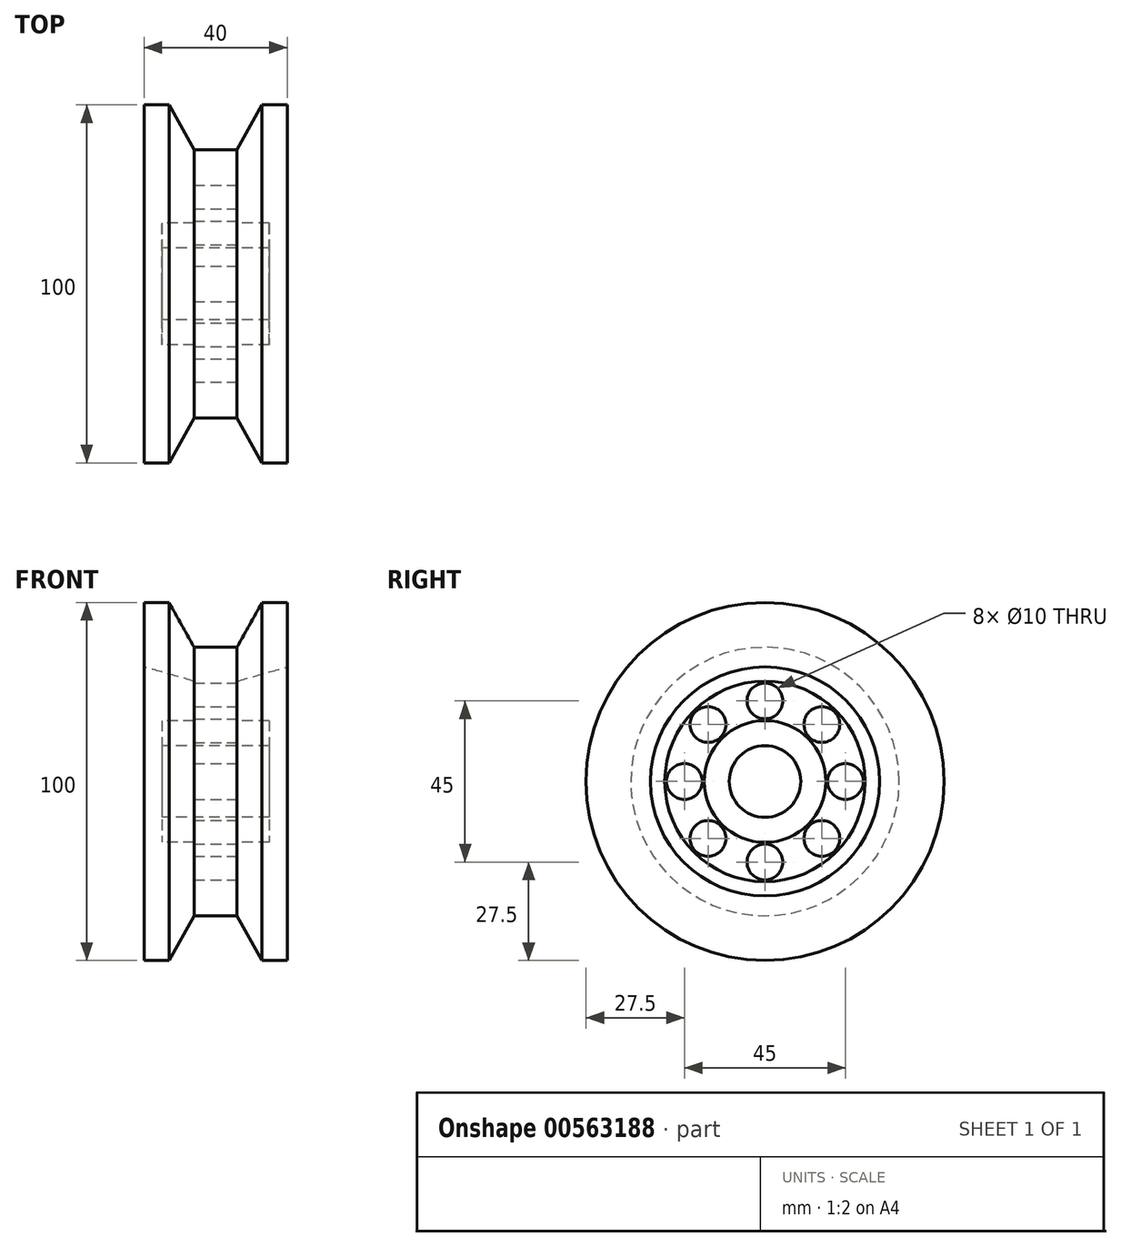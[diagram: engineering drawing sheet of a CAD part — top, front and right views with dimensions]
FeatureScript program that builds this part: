
annotation { "Feature Type Name" : "Feature", "Feature Type Description" : "" }
export const myFeature = defineFeature(function(context is Context, id is Id, definition is map)
    precondition{}
    {
        {
            var Q0;
            Q0=qCreatedBy(makeId("Front.planeOp"),FACE);
            var sketch = newSketch(context, id + "F0", { "sketchPlane" : qUnion([Q0])});
            skLineSegment(sketch, "E0", {"start": v(-20, 0) * mm, "end": v(-13, 0) * mm});
            skLineSegment(sketch, "E1", {"start": v(-20, 0) * mm, "end": v(-20, 18) * mm});
            skPoint(sketch, "E2", {"position": v(-13, 0) * mm});
            skLineSegment(sketch, "E3", {"start": v(-6, -5.42) * mm, "end": v(-6, 12.5) * mm, "construction": true});
            skPoint(sketch, "E4", {"position": v(-6, 0) * mm});
            skLineSegment(sketch, "E5", {"start": v(-13, 0) * mm, "end": v(-6, 12.5) * mm});
            skLineSegment(sketch, "E6", {"start": v(-6, 12.5) * mm, "end": v(0, 12.5) * mm});
            skLineSegment(sketch, "E7", {"start": v(-6, 12.5) * mm, "end": v(-6, 43.54) * mm, "construction": true});
            skPoint(sketch, "E8", {"position": v(-6, 22) * mm});
            skPoint(sketch, "E9", {"position": v(7.7, 57.87) * mm});
            skPoint(sketch, "E10", {"position": v(9.06, 58.61) * mm});
            skLineSegment(sketch, "E11", {"start": v(-20, 18) * mm, "end": v(-6, 22) * mm});
            skLineSegment(sketch, "E12", {"start": v(-6, 22) * mm, "end": v(0, 22) * mm});
            skLineSegment(sketch, "E13", {"start": v(-6, 22) * mm, "end": v(-6, 33) * mm});
            skLineSegment(sketch, "E14", {"start": v(-6, 33) * mm, "end": v(0, 33) * mm});
            skLineSegment(sketch, "E15", {"start": v(0, 33) * mm, "end": v(-15, 33) * mm});
            skLineSegment(sketch, "E16", {"start": v(-15, 33) * mm, "end": v(-15, 40) * mm});
            skLineSegment(sketch, "E17", {"start": v(-15, 40) * mm, "end": v(0, 40) * mm});
            skLineSegment(sketch, "E18.MirrorCS", {"start": v(15, 40) * mm, "end": v(0, 40) * mm});
            skLineSegment(sketch, "E19.MirrorCS", {"start": v(15, 33) * mm, "end": v(15, 40) * mm});
            skLineSegment(sketch, "E20.MirrorCS", {"start": v(0, 33) * mm, "end": v(15, 33) * mm});
            skLineSegment(sketch, "E21.MirrorCS", {"start": v(6, 12.5) * mm, "end": v(6, 43.54) * mm, "construction": true});
            skLineSegment(sketch, "E22.MirrorCS", {"start": v(6, 22) * mm, "end": v(0, 22) * mm});
            skLineSegment(sketch, "E23.MirrorCS", {"start": v(20, 18) * mm, "end": v(6, 22) * mm});
            skLineSegment(sketch, "E24.MirrorCS", {"start": v(6, 12.5) * mm, "end": v(0, 12.5) * mm});
            skLineSegment(sketch, "E25.MirrorCS", {"start": v(13, 0) * mm, "end": v(6, 12.5) * mm});
            skLineSegment(sketch, "E26.MirrorCS", {"start": v(20, 0) * mm, "end": v(20, 18) * mm});
            skPoint(sketch, "E27", {"position": v(6, 33) * mm});
            skLineSegment(sketch, "E28", {"start": v(6, 33) * mm, "end": v(6, 22) * mm});
            skLineSegment(sketch, "E29.trimOffspring", {"start": v(13, 0) * mm, "end": v(20, 0) * mm});
            skLineSegment(sketch, "E30", {"start": v(-64.97, 50) * mm, "end": v(56.77, 50) * mm, "construction": true});
            skPoint(sketch, "E31", {"position": v(0, 50) * mm});
            skSolve(sketch);
        }
        {
            var Q0;
            Q0=makeQuery(id+"F0.imprint","IMPRINT",FACE,{"disambiguationData":[TD([[makeQuery(id+"F0.imprint","IMPRINT",EDGE,{"derivedFrom":sQuery(id+"F0.wireOp",EDGE,"E0")}),1.0]])]});
            var Q1;
            Q1=makeQuery(id+"F0.imprint","IMPRINT",FACE,{"disambiguationData":[TD([[makeQuery(id+"F0.imprint","IMPRINT",EDGE,{"derivedFrom":sQuery(id+"F0.wireOp",EDGE,"E12")}),1.0]])]});
            var Q2;
            {var subQ0=sQuery(id+"F0.wireOp",EDGE,"E16");Q2=makeQuery(id+"F0.imprint","IMPRINT",FACE,{"disambiguationData":[TD([[makeQuery(id+"F0.imprint","IMPRINT",EDGE,{"derivedFrom":subQ0}),-1.0]])]});}
            var Q3;
            Q3=sQuery(id+"F0.wireOp",EDGE,"E30");
            revolve(context, id + "F1", {"entities" : qUnion([Q0, Q1, Q2]), "axis" : qUnion([Q3]), "revolveType" : RevolveType.FULL});
        }
        {
            var Q0;
            Q0=qCreatedBy(makeId("Right.planeOp"),FACE);
            var sketch = newSketch(context, id + "F2", { "sketchPlane" : qUnion([Q0])});
            skLineSegment(sketch, "E32", {"start": v(50, 50) * mm, "end": v(-50, 50) * mm, "construction": true});
            skLineSegment(sketch, "E33", {"start": v(0, 0) * mm, "end": v(0, 100) * mm, "construction": true});
            skPoint(sketch, "E34", {"position": v(0, 50) * mm});
            skLineSegment(sketch, "E35", {"start": v(0, 50) * mm, "end": v(-42.43, 92.43) * mm, "construction": true});
            skLineSegment(sketch, "E36.MirrorCS", {"start": v(0, 50) * mm, "end": v(42.43, 92.43) * mm, "construction": true});
            skLineSegment(sketch, "E37.MirrorCS", {"start": v(0, 50) * mm, "end": v(42.43, 7.57) * mm});
            skLineSegment(sketch, "E38.MirrorCS", {"start": v(0, 50) * mm, "end": v(-42.43, 7.57) * mm, "construction": true});
            skPoint(sketch, "E39", {"position": v(12.02, 62.02) * mm});
            skPoint(sketch, "E40", {"position": v(19.8, 69.8) * mm});
            skPoint(sketch, "E41", {"position": v(15.9, 65.9) * mm});
            skCircle(sketch, "E42", {"center": v(15.9, 65.9) * mm, "radius": 5 * mm});
            skCircle(sketch, "E43.MirrorC", {"center": v(-15.9, 65.9) * mm, "radius": 5 * mm});
            skCircle(sketch, "E44.MirrorC", {"center": v(15.9, 34.1) * mm, "radius": 5 * mm});
            skCircle(sketch, "E45.MirrorC", {"center": v(-15.9, 34.1) * mm, "radius": 5 * mm});
            skPoint(sketch, "E46", {"position": v(0, 78) * mm});
            skPoint(sketch, "E47", {"position": v(0, 72.5) * mm});
            skCircle(sketch, "E48", {"center": v(0, 72.5) * mm, "radius": 5 * mm});
            skCircle(sketch, "E49.MirrorC", {"center": v(0, 27.5) * mm, "radius": 5 * mm});
            skCircle(sketch, "E50.MirrorC", {"center": v(22.5, 50) * mm, "radius": 5 * mm});
            skCircle(sketch, "E51.MirrorC", {"center": v(-22.5, 50) * mm, "radius": 5 * mm});
            skSolve(sketch);
        }
        {
            var Q0;
            Q0=sQuery(id+"F2.wireOp",VERTEX,"E41");
            var Q1;
            Q1=sQuery(id+"F2.wireOp",VERTEX,"E47");
            var Q2;
            Q2=sQuery(id+"F2.wireOp",VERTEX,"E43.MirrorC.center");
            var Q3;
            Q3=sQuery(id+"F2.wireOp",VERTEX,"E51.MirrorC.center");
            var Q4;
            Q4=sQuery(id+"F2.wireOp",VERTEX,"E45.MirrorC.center");
            var Q5;
            Q5=sQuery(id+"F2.wireOp",VERTEX,"E49.MirrorC.center");
            var Q6;
            Q6=sQuery(id+"F2.wireOp",VERTEX,"E44.MirrorC.center");
            var Q7;
            Q7=sQuery(id+"F2.wireOp",VERTEX,"E50.MirrorC.center");
            var Q8;
            Q8=makeQuery(id+"F1.opRevolve","SWEPT_BODY",BODY,{"disambiguationData":[OSD([sQuery(id+"F0.wireOp",EDGE,"E0"),sQuery(id+"F0.wireOp",EDGE,"E1"),sQuery(id+"F0.wireOp",EDGE,"E5"),sQuery(id+"F0.wireOp",EDGE,"E6"),sQuery(id+"F0.wireOp",EDGE,"E11"),sQuery(id+"F0.wireOp",EDGE,"E13"),sQuery(id+"F0.wireOp",EDGE,"E15"),sQuery(id+"F0.wireOp",EDGE,"E16"),sQuery(id+"F0.wireOp",EDGE,"E17"),sQuery(id+"F0.wireOp",EDGE,"E18.MirrorCS"),sQuery(id+"F0.wireOp",EDGE,"E19.MirrorCS"),sQuery(id+"F0.wireOp",EDGE,"E20.MirrorCS"),sQuery(id+"F0.wireOp",EDGE,"E23.MirrorCS"),sQuery(id+"F0.wireOp",EDGE,"E24.MirrorCS"),sQuery(id+"F0.wireOp",EDGE,"E25.MirrorCS"),sQuery(id+"F0.wireOp",EDGE,"E26.MirrorCS"),sQuery(id+"F0.wireOp",EDGE,"E28"),sQuery(id+"F0.wireOp",EDGE,"E29.trimOffspring")])]});
            hole(context, id + "F3", {"style" : HoleStyle.SIMPLE, "endStyle" : HoleEndStyle.THROUGH, "holeDiameter" : 10 * mm, "isTappedThrough" : true, "tappedDepth" : 12 * mm, "tapClearance" : 3, "locations" : qUnion([Q0, Q1, Q2, Q3, Q4, Q5, Q6, Q7]), "scope" : qUnion([Q8])});
        }
        {
            var Q0;
            Q0=sQuery(id+"F2.wireOp",VERTEX,"E47");
            var Q1;
            Q1=sQuery(id+"F2.wireOp",VERTEX,"E41");
            var Q2;
            Q2=sQuery(id+"F2.wireOp",VERTEX,"E50.MirrorC.center");
            var Q3;
            Q3=sQuery(id+"F2.wireOp",VERTEX,"E44.MirrorC.center");
            var Q4;
            Q4=sQuery(id+"F2.wireOp",VERTEX,"E49.MirrorC.center");
            var Q5;
            Q5=sQuery(id+"F2.wireOp",VERTEX,"E45.MirrorC.center");
            var Q6;
            Q6=sQuery(id+"F2.wireOp",VERTEX,"E51.MirrorC.center");
            var Q7;
            Q7=sQuery(id+"F2.wireOp",VERTEX,"E43.MirrorC.center");
            var Q8;
            Q8=makeQuery(id+"F1.opRevolve","SWEPT_BODY",BODY,{"disambiguationData":[OSD([sQuery(id+"F0.wireOp",EDGE,"E0"),sQuery(id+"F0.wireOp",EDGE,"E1"),sQuery(id+"F0.wireOp",EDGE,"E5"),sQuery(id+"F0.wireOp",EDGE,"E6"),sQuery(id+"F0.wireOp",EDGE,"E11"),sQuery(id+"F0.wireOp",EDGE,"E13"),sQuery(id+"F0.wireOp",EDGE,"E15"),sQuery(id+"F0.wireOp",EDGE,"E16"),sQuery(id+"F0.wireOp",EDGE,"E17"),sQuery(id+"F0.wireOp",EDGE,"E18.MirrorCS"),sQuery(id+"F0.wireOp",EDGE,"E19.MirrorCS"),sQuery(id+"F0.wireOp",EDGE,"E20.MirrorCS"),sQuery(id+"F0.wireOp",EDGE,"E23.MirrorCS"),sQuery(id+"F0.wireOp",EDGE,"E24.MirrorCS"),sQuery(id+"F0.wireOp",EDGE,"E25.MirrorCS"),sQuery(id+"F0.wireOp",EDGE,"E26.MirrorCS"),sQuery(id+"F0.wireOp",EDGE,"E28"),sQuery(id+"F0.wireOp",EDGE,"E29.trimOffspring")])]});
            hole(context, id + "F4", {"style" : HoleStyle.SIMPLE, "endStyle" : HoleEndStyle.THROUGH, "oppositeDirection" : true, "holeDiameter" : 10 * mm, "isTappedThrough" : true, "tappedDepth" : 12 * mm, "tapClearance" : 3, "locations" : qUnion([Q0, Q1, Q2, Q3, Q4, Q5, Q6, Q7]), "scope" : qUnion([Q8])});
        }
    });
